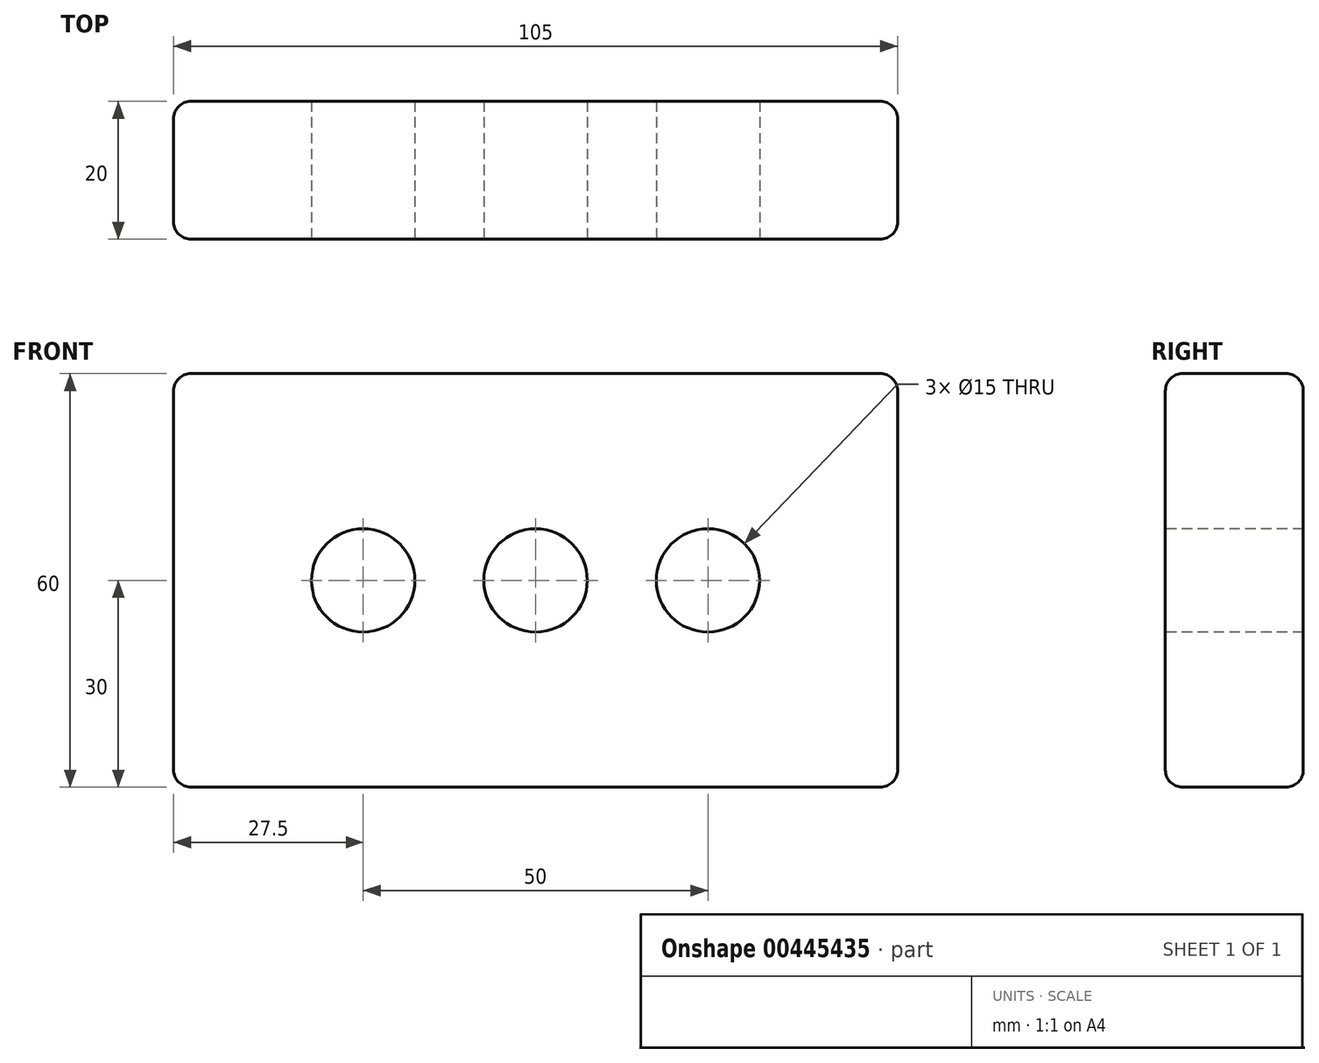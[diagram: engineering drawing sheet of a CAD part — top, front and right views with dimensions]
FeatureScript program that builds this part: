
annotation { "Feature Type Name" : "Feature", "Feature Type Description" : "" }
export const myFeature = defineFeature(function(context is Context, id is Id, definition is map)
    precondition{}
    {
        {
            var Q0;
            Q0=qCreatedBy(makeId("Front.planeOp"),FACE);
            var sketch = newSketch(context, id + "F0", { "sketchPlane" : qUnion([Q0])});
            skLineSegment(sketch, "E0.bottom", {"start": v(-52.5, -30) * mm, "end": v(52.5, -30) * mm});
            skLineSegment(sketch, "E0.top", {"start": v(-52.5, 30) * mm, "end": v(52.5, 30) * mm});
            skLineSegment(sketch, "E0.left", {"start": v(-52.5, -30) * mm, "end": v(-52.5, 30) * mm});
            skLineSegment(sketch, "E0.right", {"start": v(52.5, -30) * mm, "end": v(52.5, 30) * mm});
            skPoint(sketch, "E0.middle", {"position": v(0, 0) * mm});
            skCircle(sketch, "E1", {"center": v(0, 0) * mm, "radius": 7.5 * mm});
            skLineSegment(sketch, "E2", {"start": v(-7.5, 0) * mm, "end": v(-25, 0) * mm});
            skLineSegment(sketch, "E3", {"start": v(7.5, 0) * mm, "end": v(25, 0) * mm});
            skCircle(sketch, "E4", {"center": v(-25, 0) * mm, "radius": 7.5 * mm});
            skCircle(sketch, "E5", {"center": v(25, 0) * mm, "radius": 7.5 * mm});
            skSolve(sketch);
        }
        {
            var Q0;
            Q0 = qSketchRegion(id + "F0", true);
            extrude(context, id + "F1", {"entities" : qUnion([Q0]), "oppositeDirection" : true, "depth" : 20 * mm});
        }
        {
            var Q0;
            Q0=makeQuery(id+"F1.opExtrude","CAP_EDGE",EDGE,{"disambiguationData":[OSD([sQuery(id+"F0.wireOp",EDGE,"E0.left")])],"isStart":true});
            var Q1;
            Q1=makeQuery(id+"F1.opExtrude","CAP_EDGE",EDGE,{"disambiguationData":[OSD([sQuery(id+"F0.wireOp",EDGE,"E0.top")])],"isStart":true});
            var Q2;
            Q2=makeQuery(id+"F1.opExtrude","CAP_EDGE",EDGE,{"disambiguationData":[OSD([sQuery(id+"F0.wireOp",EDGE,"E0.bottom")])],"isStart":true});
            var Q3;
            Q3=makeQuery(id+"F1.opExtrude","CAP_EDGE",EDGE,{"disambiguationData":[OSD([sQuery(id+"F0.wireOp",EDGE,"E0.right")])],"isStart":true});
            var Q4;
            Q4=makeQuery(id+"F1.opExtrude","SWEPT_EDGE",EDGE,{"disambiguationData":[OSD([sQuery(id+"F0.wireOp",EDGE,"E0.top"),sQuery(id+"F0.wireOp",EDGE,"E0.right")])]});
            var Q5;
            Q5=makeQuery(id+"F1.opExtrude","SWEPT_EDGE",EDGE,{"disambiguationData":[OSD([sQuery(id+"F0.wireOp",EDGE,"E0.top"),sQuery(id+"F0.wireOp",EDGE,"E0.left")])]});
            var Q6;
            Q6=makeQuery(id+"F1.opExtrude","CAP_EDGE",EDGE,{"disambiguationData":[OSD([sQuery(id+"F0.wireOp",EDGE,"E0.top")])],"isStart":false});
            var Q7;
            Q7=makeQuery(id+"F1.opExtrude","CAP_EDGE",EDGE,{"disambiguationData":[OSD([sQuery(id+"F0.wireOp",EDGE,"E0.right")])],"isStart":false});
            var Q8;
            Q8=makeQuery(id+"F1.opExtrude","SWEPT_EDGE",EDGE,{"disambiguationData":[OSD([sQuery(id+"F0.wireOp",EDGE,"E0.bottom"),sQuery(id+"F0.wireOp",EDGE,"E0.right")])]});
            var Q9;
            Q9=makeQuery(id+"F1.opExtrude","CAP_EDGE",EDGE,{"disambiguationData":[OSD([sQuery(id+"F0.wireOp",EDGE,"E0.bottom")])],"isStart":false});
            var Q10;
            Q10=makeQuery(id+"F1.opExtrude","CAP_EDGE",EDGE,{"disambiguationData":[OSD([sQuery(id+"F0.wireOp",EDGE,"E0.left")])],"isStart":false});
            var Q11;
            Q11=makeQuery(id+"F1.opExtrude","SWEPT_EDGE",EDGE,{"disambiguationData":[OSD([sQuery(id+"F0.wireOp",EDGE,"E0.bottom"),sQuery(id+"F0.wireOp",EDGE,"E0.left")])]});
            fillet(context, id + "F2", {"entities" : qUnion([Q0, Q1, Q2, Q3, Q4, Q5, Q6, Q7, Q8, Q9, Q10, Q11]), "radius" : 2.5 * mm, "tangentPropagation" : true, "allowEdgeOverflow" : false});
        }
    });
